# Revit family: Shelf-Bradley_Corp-790
name_source: partatom
category: Specialty Equipment
revit_build: Autodesk Revit MEP 2012 (Build: 20110309_2315(x64)
units: mm (PartAtom-declared; Revit-internal decimal feet)

## types (1)
- 790
    ADA Compliant = No
    Assembly Code = C1030200
    Buy American Act = To Be Determined
    Default Elevation = 4' - 0"
    Depth = 0' - 0 3/8"
    Description = Fold-Down Utility Shelf
    Height = 1' - 5 1/2"
    Low Emitting Material = No
    Manufacturer = Bradley Corporation
    MasterFormat Number = 10 28 13
    MasterFormat Title = Toilet Accessories
    Model = 790
    OmniClass Code = 23.40.20.27.11
    OmniClass Title = Storage Shelving
    Percentage of Recycled Content = 0
    Product Tech Data URL - English = http://bradleycorp.com
    Product Tech Data URL - French = http://bradleycorp.com
    Product Tech Data URL - Spanish = http://bradleycorp.com
    Shelf And Mounting Bracket Material = Metal - Bradley Corp - Chrome
    Specifications URL = http://www.bradleycorp.com
    URL = http://www.bradleycorp.com
    Version = 2.0
    Warranty Information = Complete unit, one year.
    Width = 0' - 5 1/2"

## geometry (parser evidence)
native form markers: Blend x2, Sweep x2
no freeform markers — native parametric forms only
